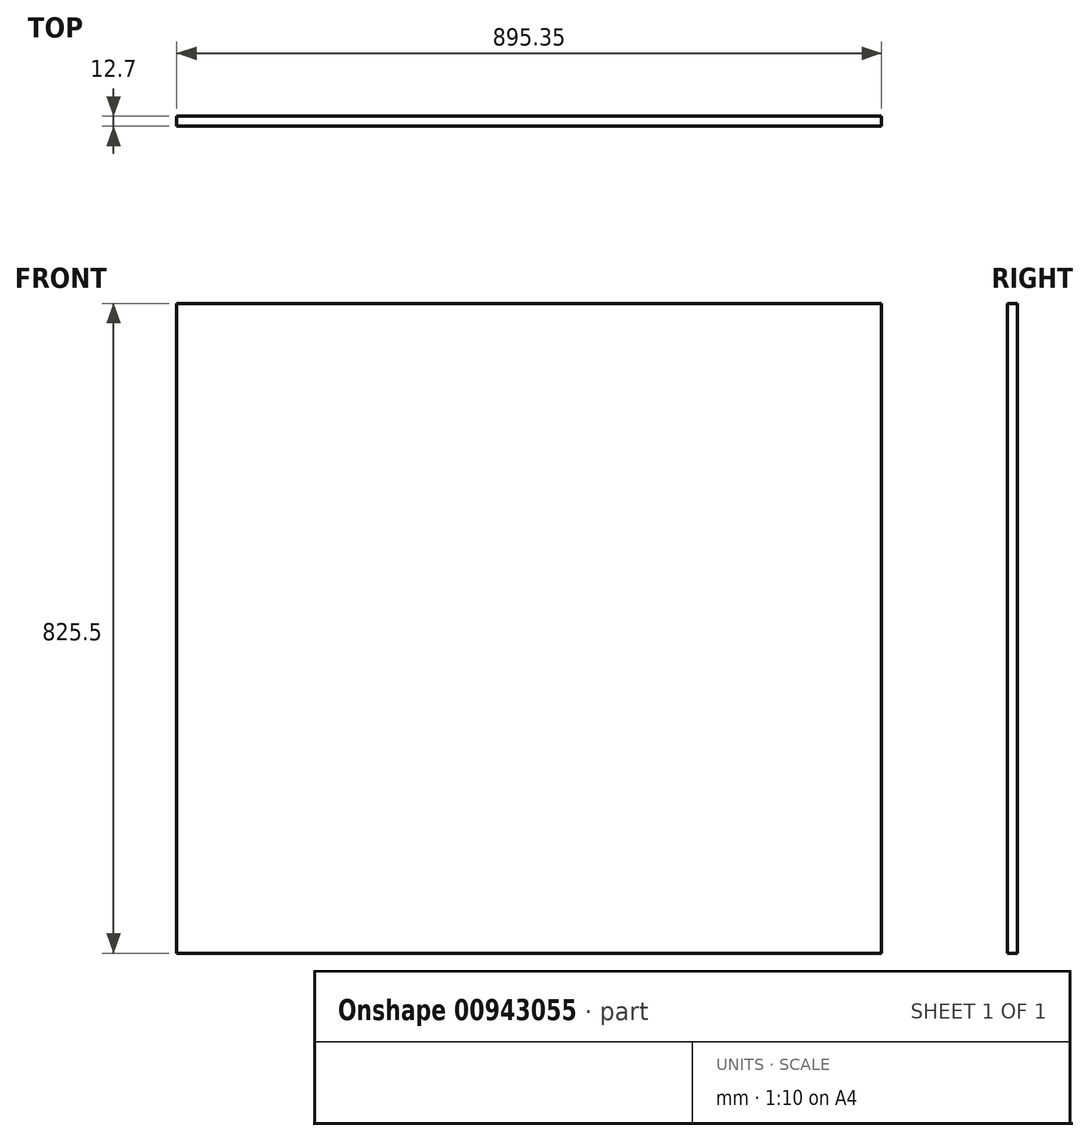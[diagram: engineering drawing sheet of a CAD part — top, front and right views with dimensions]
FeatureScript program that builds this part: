
annotation { "Feature Type Name" : "Feature", "Feature Type Description" : "" }
export const myFeature = defineFeature(function(context is Context, id is Id, definition is map)
    precondition{}
    {
        {
            var Q0;
            Q0=qCreatedBy(makeId("Front.planeOp"),FACE);
            var sketch = newSketch(context, id + "F0", { "sketchPlane" : qUnion([Q0])});
            skLineSegment(sketch, "E0.bottom", {"start": v(0, 0) * mm, "end": v(895.35, 0) * mm});
            skLineSegment(sketch, "E0.top", {"start": v(0, 825.5) * mm, "end": v(895.35, 825.5) * mm});
            skLineSegment(sketch, "E0.left", {"start": v(0, 0) * mm, "end": v(0, 825.5) * mm});
            skLineSegment(sketch, "E0.right", {"start": v(895.35, 0) * mm, "end": v(895.35, 825.5) * mm});
            skSolve(sketch);
        }
        {
            var Q0;
            Q0=makeQuery(id+"F0.imprint","IMPRINT",FACE,{"disambiguationData":[TD([[makeQuery(id+"F0.imprint","IMPRINT",EDGE,{"derivedFrom":sQuery(id+"F0.wireOp",EDGE,"E0.bottom")}),1.0]])]});
            extrude(context, id + "F1", {"entities" : qUnion([Q0]), "depth" : 12.7 * mm, "offsetDistance" : 25.4 * mm});
        }
    });
